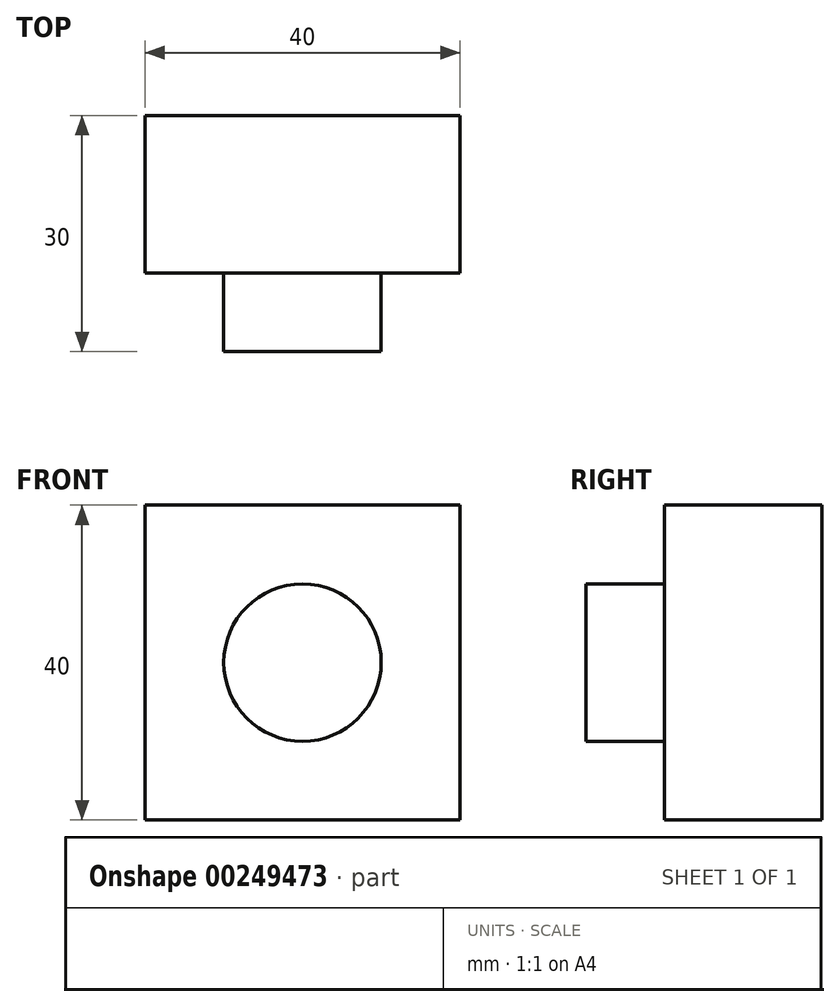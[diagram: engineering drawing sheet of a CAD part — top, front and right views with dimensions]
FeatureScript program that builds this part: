
annotation { "Feature Type Name" : "Feature", "Feature Type Description" : "" }
export const myFeature = defineFeature(function(context is Context, id is Id, definition is map)
    precondition{}
    {
        {
            var Q0;
            Q0=qCreatedBy(makeId("Front.planeOp"),FACE);
            var sketch = newSketch(context, id + "F0", { "sketchPlane" : qUnion([Q0])});
            skLineSegment(sketch, "E0.bottom", {"start": v(20, -20) * mm, "end": v(-20, -20) * mm});
            skLineSegment(sketch, "E0.top", {"start": v(20, 20) * mm, "end": v(-20, 20) * mm});
            skLineSegment(sketch, "E0.left", {"start": v(20, -20) * mm, "end": v(20, 20) * mm});
            skLineSegment(sketch, "E0.right", {"start": v(-20, -20) * mm, "end": v(-20, 20) * mm});
            skPoint(sketch, "E0.middle", {"position": v(0, 0) * mm});
            skSolve(sketch);
        }
        {
            var Q0;
            Q0=makeQuery(id+"F0.imprint","IMPRINT",FACE,{"disambiguationData":[TD([[makeQuery(id+"F0.imprint","IMPRINT",EDGE,{"derivedFrom":sQuery(id+"F0.wireOp",EDGE,"E0.bottom")}),-1.0]])]});
            extrude(context, id + "F1", {"entities" : qUnion([Q0]), "depth" : 20 * mm});
        }
        {
            var Q0;
            Q0=makeQuery(id+"F1.opExtrude","CAP_FACE",FACE,{"disambiguationData":[OSD([sQuery(id+"F0.wireOp",EDGE,"E0.bottom"),sQuery(id+"F0.wireOp",EDGE,"E0.top"),sQuery(id+"F0.wireOp",EDGE,"E0.left"),sQuery(id+"F0.wireOp",EDGE,"E0.right")])],"isStart":false});
            var sketch = newSketch(context, id + "F2", { "sketchPlane" : qUnion([Q0])});
            skCircle(sketch, "E1", {"center": v(0, 0) * mm, "radius": 10 * mm});
            skSolve(sketch);
        }
        {
            var Q0;
            Q0=makeQuery(id+"F2.imprint","IMPRINT",FACE,{"disambiguationData":[TD([[makeQuery(id+"F2.imprint","IMPRINT",EDGE,{"derivedFrom":sQuery(id+"F2.wireOp",EDGE,"E1")}),1.0]])]});
            extrude(context, id + "F3", {"entities" : qUnion([Q0]), "operationType" : NewBodyOperationType.ADD, "depth" : 10 * mm});
        }
    });
